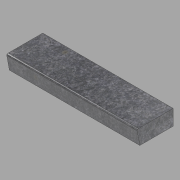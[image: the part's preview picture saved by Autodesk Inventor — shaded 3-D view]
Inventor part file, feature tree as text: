
AUTODESK INVENTOR PART (.ipt)
format: ipt  version: 2022.1 (Build 261234020, 234B)  size: 102,912 bytes
history: native  units: in
note: dims shown in document units (in); Inventor stores cm internally (conversion verified against a paired STEP export)
features: extrude x1, sketch x1
ambient origin geometry x8: Origin, YZ Plane, XZ Plane, XY Plane, X Axis, Y Axis, Z Axis, Center Point
bodies: Solid1 (feature_tree)
feature tree (2):
  extrude  "Extrusion1"  Depth=50.8in TaperAngle=0.0deg
  sketch  "Sketch2"  dims[d0=6.0in d11=50.8in d12=0.0in d14=13.5in d15=13.0in d16=0.5in d17=5.5in]
